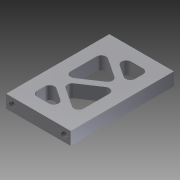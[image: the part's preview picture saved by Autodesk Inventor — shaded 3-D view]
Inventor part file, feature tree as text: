
AUTODESK INVENTOR PART (.ipt)
format: ipt  version: 2012 (Build 160160000, 160)  size: 193,536 bytes
history: native  units: in
note: dims shown in document units (in); Inventor stores cm internally (conversion verified against a paired STEP export)
features: extrude x6, sketch x5, thread x4, plane x1, fillet x1, hole x1
ambient origin geometry x8: Origin, YZ Plane, XZ Plane, XY Plane, X Axis, Y Axis, Z Axis, Center Point
bodies: Solid1 (feature_tree)
feature tree (18):
  sketch  "Sketch1"  dims[d0=0.25in d1=1.25in]
  extrude  "Extrusion1"  Depth=1.25in
  sketch  "Sketch2"  dims[d2=2.0in d3=0.0in d4=0.125in]
  plane  "Work Plane1"
  sketch  "Sketch3"  dims[d5=0.125in d6=0.125in]
  extrude  "Extrusion4"  Depth=0.125in
  sketch  "Sketch5"  dims[d8=0.125in d26=-0.125in]
  extrude  "Extrusion6"  Depth=0.125in
  sketch  "Sketch6"  dims[d27=0.25in d28=0.25in d29=0.25in d30=0.25in d31=0.2315in d32=0.463in d33=0.0625in d34=0.125in d35=0.0625in d36=0.125in d37=0.0625in d38=0.125in d47=1.0in d48=0.0in d52=0.0625in d53=0.0in d56=0.0625in d57=0.0in d71=0.25in d72=0.0in d73=0.0938in d74=0.5in d75=0.0in d76=0.125in d77=0.75in d78=0.375in d79=0.25in d80=0.5635in d81=0.5in d82=0.8108in d83=1.0in d84=0.0in d85=1.0in d86=0.0in d87=1.0in d88=0.0in d89=1.0in d90=0.0in]
  extrude  "Extrusion8"  [1 undecoded]
  extrude  "Extrusion11"  Depth=0.25in
  fillet  "Fillet7"  Radius=0.25in
  extrude  "Extrusion12"  Depth=0.25in
  hole  "Hole2"  [1 undecoded]
  thread  "Thread5"  [1 undecoded]
  thread  "Thread6"  [1 undecoded]
  thread  "Thread7"  [1 undecoded]
  thread  "Thread8"  [1 undecoded]
note: 6 required parameter values undecoded (feature->parameter linkage not recoverable at this tier; creation-order binding heuristic only, values carry confidence <= 0.55)
